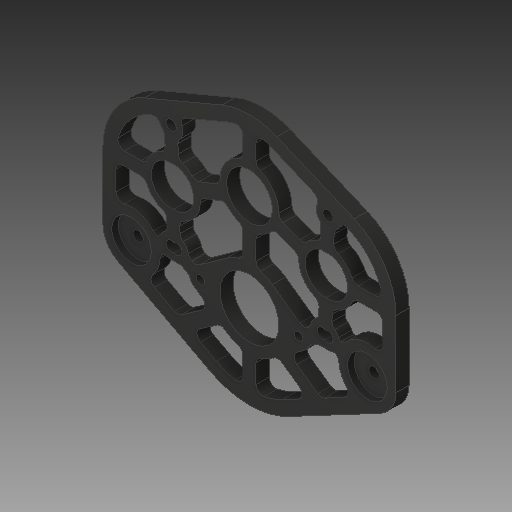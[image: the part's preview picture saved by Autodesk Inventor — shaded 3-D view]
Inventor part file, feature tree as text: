
AUTODESK INVENTOR PART (.ipt)
format: ipt  version: 2018 (Build 220112000, 112)  size: 335,360 bytes
history: native  units: in
note: dims shown in document units (in); Inventor stores cm internally (conversion verified against a paired STEP export)
features: mirror x1
ambient origin geometry x8: Origin, YZ Plane, XZ Plane, XY Plane, X Axis, Y Axis, Z Axis, Center Point
bodies: Solid1 (feature_tree)
feature tree (1):
  mirror  "Mirror1"
